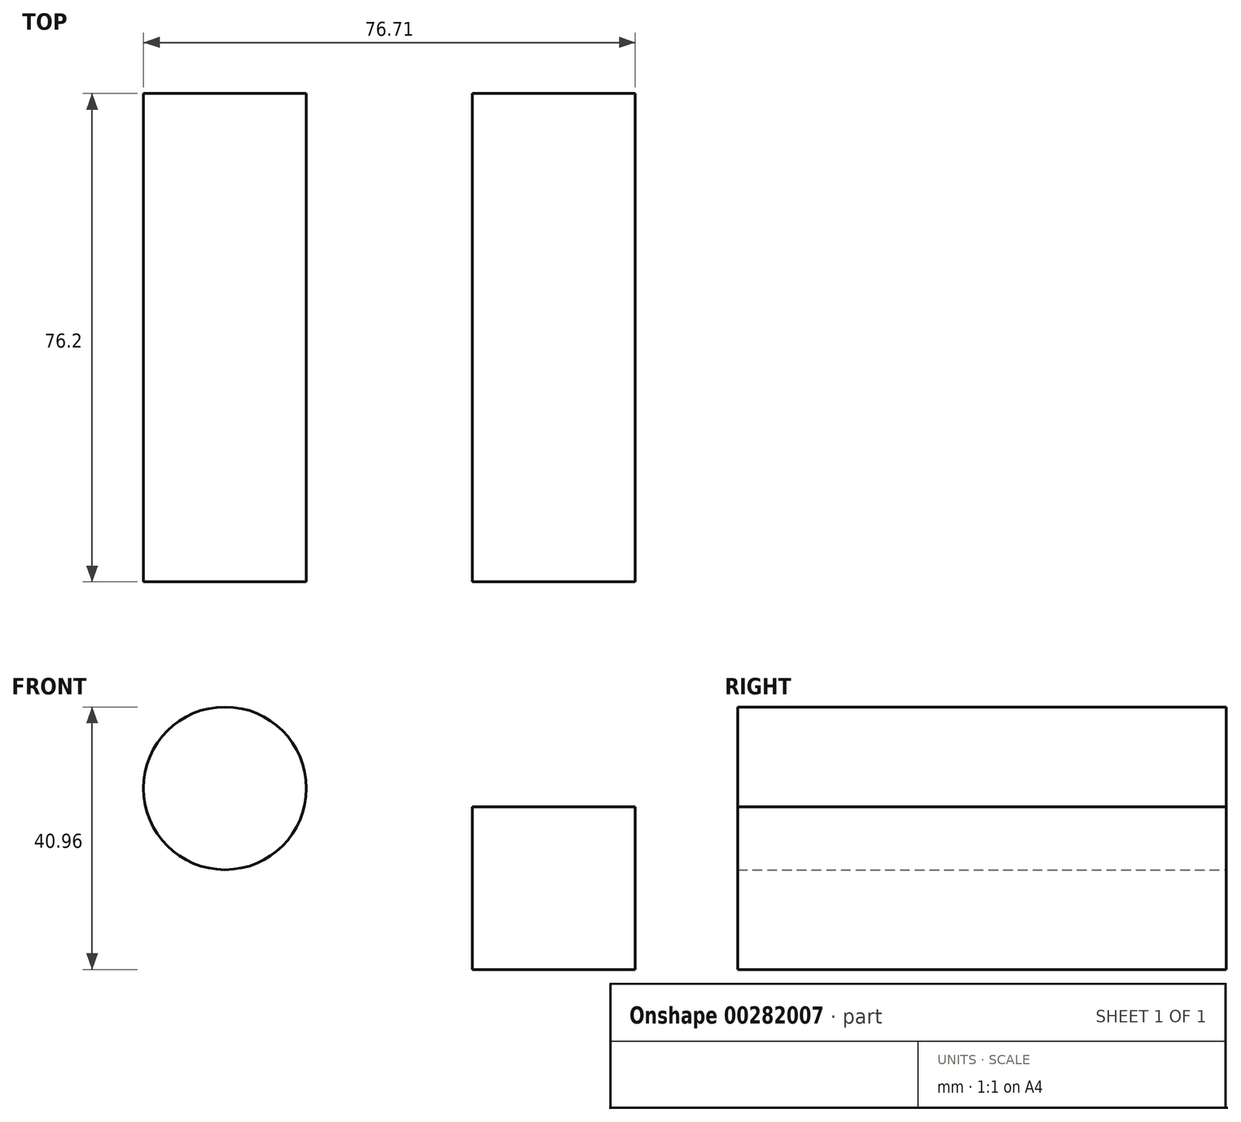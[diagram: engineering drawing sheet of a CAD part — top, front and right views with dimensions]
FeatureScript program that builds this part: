
annotation { "Feature Type Name" : "Feature", "Feature Type Description" : "" }
export const myFeature = defineFeature(function(context is Context, id is Id, definition is map)
    precondition{}
    {
        {
            var Q0;
            Q0=qCreatedBy(makeId("Front.planeOp"),FACE);
            var sketch = newSketch(context, id + "F0", { "sketchPlane" : qUnion([Q0])});
            skCircle(sketch, "E0", {"center": v(-38.61, 28.26) * mm, "radius": 12.7 * mm});
            skLineSegment(sketch, "E1.bottom", {"start": v(0, 0) * mm, "end": v(25.4, 0) * mm});
            skLineSegment(sketch, "E1.top", {"start": v(0, 25.4) * mm, "end": v(25.4, 25.4) * mm});
            skLineSegment(sketch, "E1.left", {"start": v(0, 0) * mm, "end": v(0, 25.4) * mm});
            skLineSegment(sketch, "E1.right", {"start": v(25.4, 0) * mm, "end": v(25.4, 25.4) * mm});
            skSolve(sketch);
        }
        {
            var Q0;
            Q0 = qSketchRegion(id + "F0", true);
            extrude(context, id + "F1", {"entities" : qUnion([Q0]), "depth" : 76.2 * mm});
        }
    });
